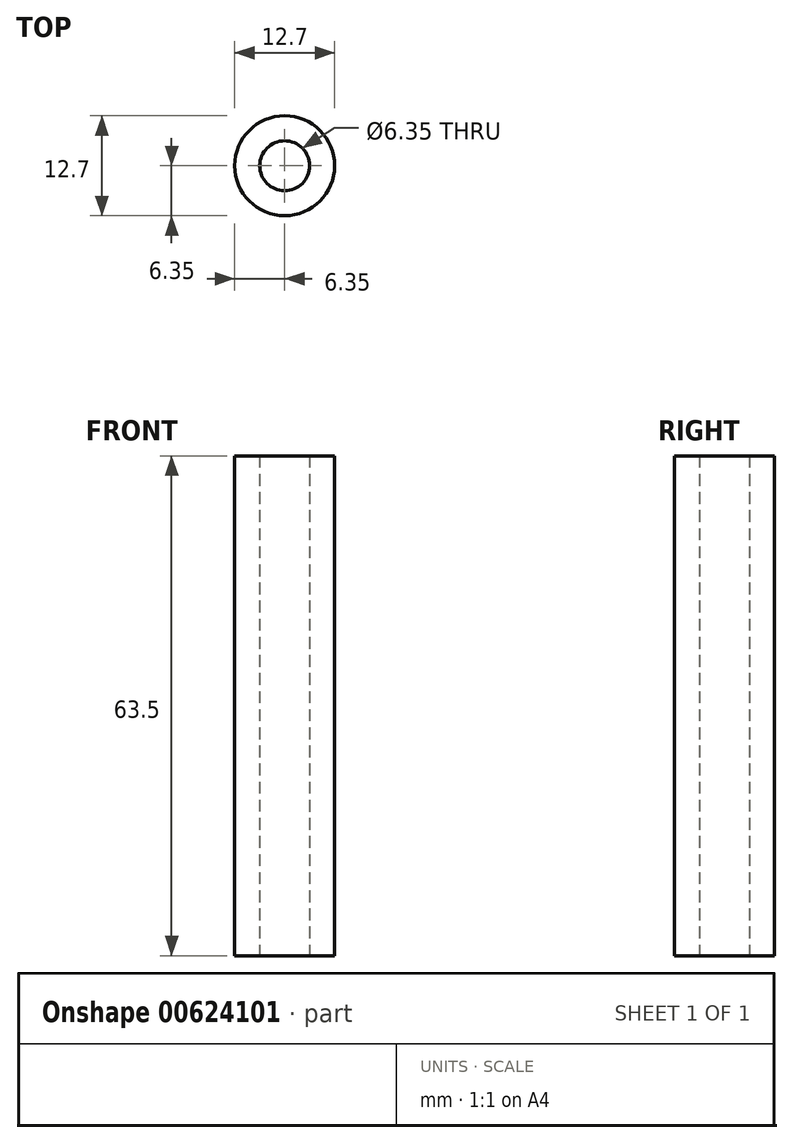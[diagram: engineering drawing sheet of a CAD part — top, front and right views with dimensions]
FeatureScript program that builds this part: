
annotation { "Feature Type Name" : "Feature", "Feature Type Description" : "" }
export const myFeature = defineFeature(function(context is Context, id is Id, definition is map)
    precondition{}
    {
        {
            var Q0;
            Q0=qCreatedBy(makeId("Top.planeOp"),FACE);
            var sketch = newSketch(context, id + "F0", { "sketchPlane" : qUnion([Q0])});
            skCircle(sketch, "E0", {"center": v(0, 0) * mm, "radius": 6.35 * mm});
            skCircle(sketch, "E1", {"center": v(0, 0) * mm, "radius": 3.18 * mm});
            skSolve(sketch);
        }
        {
            var Q0;
            Q0=makeQuery(id+"F0.imprint","IMPRINT",FACE,{"disambiguationData":[TD([[makeQuery(id+"F0.imprint","IMPRINT",EDGE,{"derivedFrom":sQuery(id+"F0.wireOp",EDGE,"E0")}),1.0]])]});
            extrude(context, id + "F1", {"entities" : qUnion([Q0]), "depth" : 63.5 * mm, "offsetDistance" : 25.4 * mm});
        }
    });
